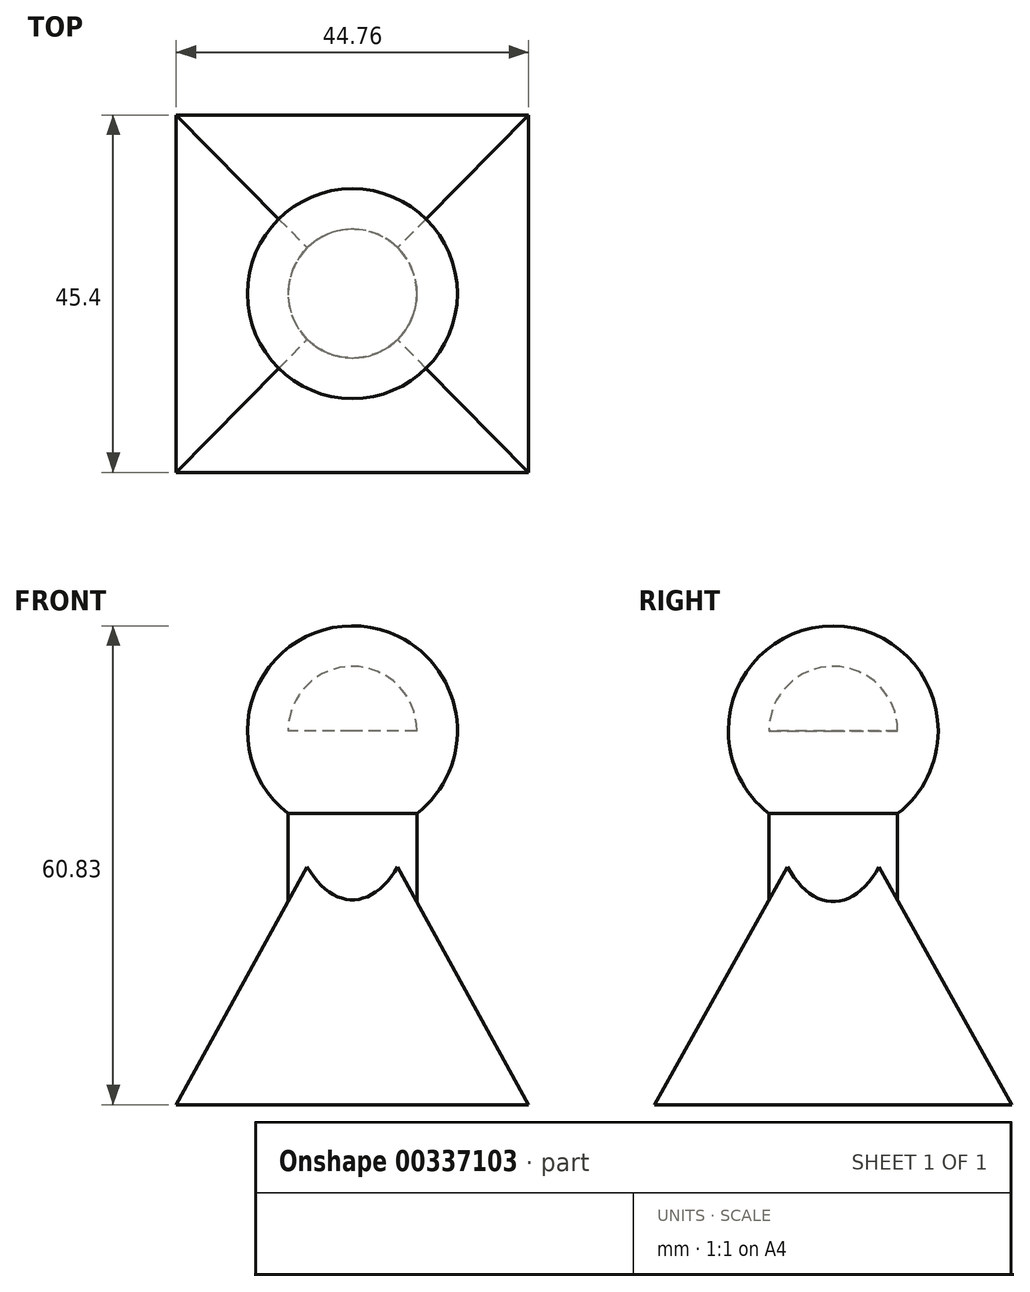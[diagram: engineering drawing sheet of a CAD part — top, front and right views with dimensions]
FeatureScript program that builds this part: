
annotation { "Feature Type Name" : "Feature", "Feature Type Description" : "" }
export const myFeature = defineFeature(function(context is Context, id is Id, definition is map)
    precondition{}
    {
        {
            var Q0;
            Q0=qCreatedBy(makeId("Top.planeOp"),FACE);
            cPlane(context, id + "F0", {"entities" : qUnion([Q0]), "cplaneType" : CPlaneType.OFFSET, "offset" : 40.64 * mm, "width" : 152.4 * mm, "height" : 152.4 * mm});
        }
        {
            var Q0;
            Q0=qCreatedBy(makeId("Top.planeOp"),FACE);
            var sketch = newSketch(context, id + "F1", { "sketchPlane" : qUnion([Q0])});
            skLineSegment(sketch, "E0.bottom", {"start": v(22.38, 22.7) * mm, "end": v(-22.38, 22.7) * mm});
            skLineSegment(sketch, "E0.top", {"start": v(22.38, -22.7) * mm, "end": v(-22.38, -22.7) * mm});
            skLineSegment(sketch, "E0.left", {"start": v(22.38, 22.7) * mm, "end": v(22.38, -22.7) * mm});
            skLineSegment(sketch, "E0.right", {"start": v(-22.38, 22.7) * mm, "end": v(-22.38, -22.7) * mm});
            skPoint(sketch, "E0.middle", {"position": v(0, 0) * mm});
            skSolve(sketch);
        }
        {
            var Q0;
            Q0=qCreatedBy(id+"F0.planeOp",FACE);
            var sketch = newSketch(context, id + "F2", { "sketchPlane" : qUnion([Q0])});
            skPoint(sketch, "E1", {"position": v(0, 0) * mm});
            skCircle(sketch, "E2", {"center": v(0, 0) * mm, "radius": 8.17 * mm});
            skSolve(sketch);
        }
        {
            var Q0;
            Q0=makeQuery(id+"F1.imprint","IMPRINT",FACE,{"disambiguationData":[TD([[makeQuery(id+"F1.imprint","IMPRINT",EDGE,{"derivedFrom":sQuery(id+"F1.wireOp",EDGE,"E0.bottom")}),1.0]])]});
            var Q1;
            Q1=sQuery(id+"F2.wireOp",VERTEX,"E1");
            loft(context, id + "F3", {"sheetProfilesArray" : [{ "sheetProfileEntities" : qUnion([Q0]) }, { "sheetProfileEntities" : qUnion([Q1]) }]});
        }
        {
            var Q0;
            Q0 = qSketchRegion(id + "F2", true);
            extrude(context, id + "F4", {"entities" : qUnion([Q0]), "operationType" : NewBodyOperationType.ADD, "depth" : 6.86 * mm, "hasSecondDirection" : true, "secondDirectionOppositeDirection" : true, "secondDirectionDepth" : 30.48 * mm});
        }
        {
            var Q0;
            Q0=makeQuery(id+"F4.opExtrude","CAP_FACE",FACE,{"disambiguationData":[OSD([sQuery(id+"F2.wireOp",EDGE,"E2")])],"isStart":false});
            var sketch = newSketch(context, id + "F5", { "sketchPlane" : qUnion([Q0])});
            skCircle(sketch, "E3", {"center": v(0, 0) * mm, "radius": 13.33 * mm});
            skLineSegment(sketch, "E4", {"start": v(0, 13.33) * mm, "end": v(0, -13.33) * mm});
            skSolve(sketch);
        }
        {
            var Q0;
            {var subQ0=sQuery(id+"F5.wireOp",EDGE,"E4");var subQ1=sQuery(id+"F5.wireOp",EDGE,"E3");var subQ2=makeQuery(id+"F5.imprint","INTERSECT",VERTEX,{"disambiguationData":[OD(0.0)],"derivedFrom":[subQ1,subQ0]});Q0=makeQuery(id+"F5.imprint","IMPRINT",FACE,{"disambiguationData":[TD([[makeQuery(id+"F5.imprint","IMPRINT",EDGE,{"disambiguationData":[TD([[subQ2,1.0]])],"derivedFrom":subQ1}),1.0]])]});}
            var Q1;
            Q1=sQuery(id+"F5.wireOp",EDGE,"E4");
            revolve(context, id + "F6", {"operationType" : NewBodyOperationType.ADD, "entities" : qUnion([Q0]), "axis" : qUnion([Q1]), "revolveType" : RevolveType.FULL});
        }
    });
